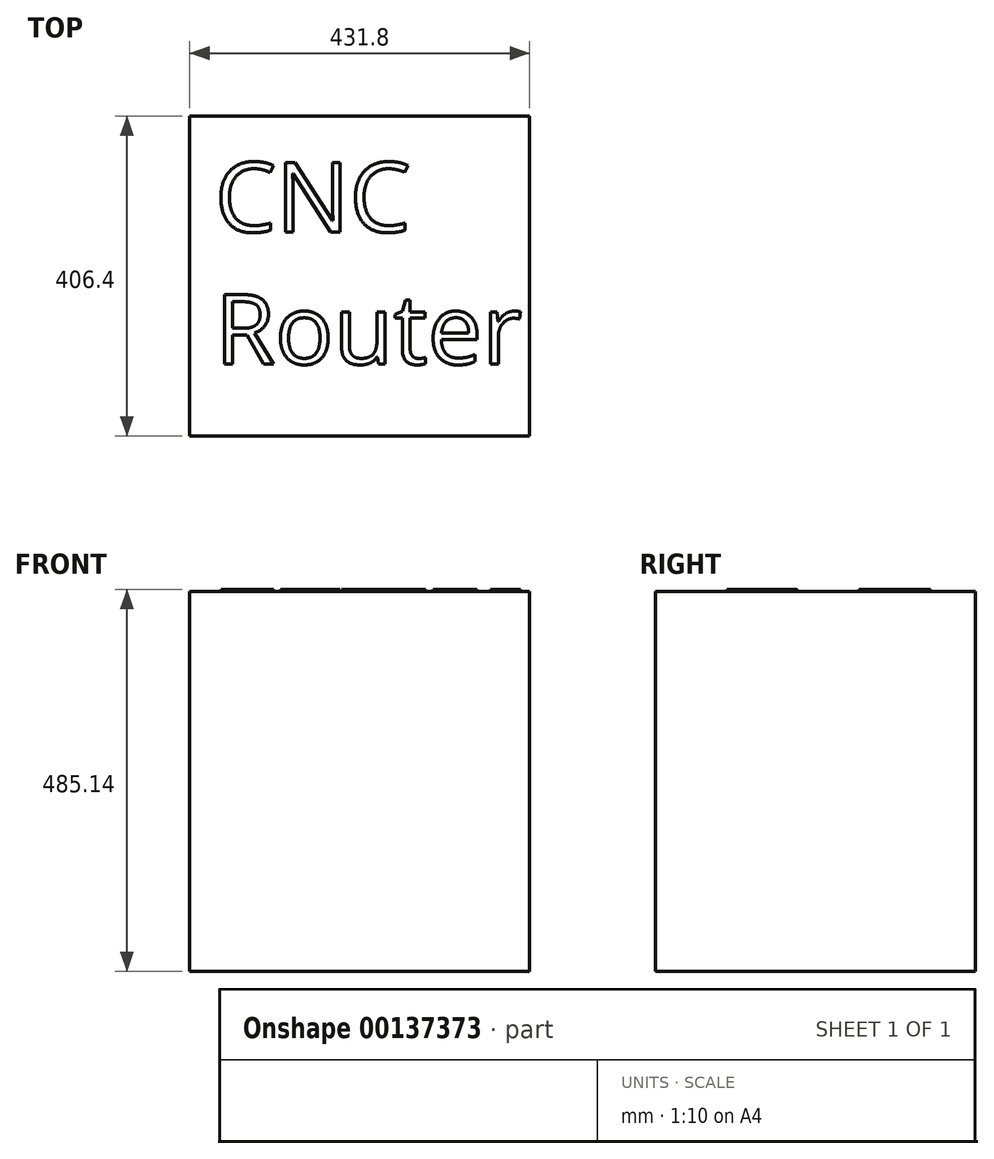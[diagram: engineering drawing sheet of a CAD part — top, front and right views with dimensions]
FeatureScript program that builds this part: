
annotation { "Feature Type Name" : "Feature", "Feature Type Description" : "" }
export const myFeature = defineFeature(function(context is Context, id is Id, definition is map)
    precondition{}
    {
        {
            var Q0;
            Q0=qCreatedBy(makeId("Top.planeOp"),FACE);
            var sketch = newSketch(context, id + "F0", { "sketchPlane" : qUnion([Q0])});
            skLineSegment(sketch, "E0.bottom", {"start": v(-209.66, 203.2) * mm, "end": v(222.14, 203.2) * mm});
            skLineSegment(sketch, "E0.top", {"start": v(-209.66, -203.2) * mm, "end": v(222.14, -203.2) * mm});
            skLineSegment(sketch, "E0.left", {"start": v(-209.66, 203.2) * mm, "end": v(-209.66, -203.2) * mm});
            skLineSegment(sketch, "E0.right", {"start": v(222.14, 203.2) * mm, "end": v(222.14, -203.2) * mm});
            skPoint(sketch, "E0.middle", {"position": v(6.24, 0) * mm});
            skSolve(sketch);
        }
        {
            var Q0;
            Q0 = qSketchRegion(id + "F0", true);
            extrude(context, id + "F1", {"entities" : qUnion([Q0]), "depth" : 482.6 * mm});
        }
        {
            var Q0;
            Q0=makeQuery(id+"F1.opExtrude","CAP_FACE",FACE,{"disambiguationData":[OSD([sQuery(id+"F0.wireOp",EDGE,"E0.bottom"),sQuery(id+"F0.wireOp",EDGE,"E0.top"),sQuery(id+"F0.wireOp",EDGE,"E0.left"),sQuery(id+"F0.wireOp",EDGE,"E0.right")])],"isStart":false});
            var sketch = newSketch(context, id + "F2", { "sketchPlane" : qUnion([Q0])});
            skText(sketch, "E1", { "text": "CNC \nRouter", "fontName": "OpenSans-Regular.ttf"});
            const initialGuessF2  = {"E1": [-0.1778, 0.05615, 1, 0, 0.0889]};
            skSetInitialGuess(sketch, initialGuessF2);
            skSolve(sketch);
        }
        {
            var Q0;
            Q0 = qSketchRegion(id + "F2", true);
            extrude(context, id + "F3", {"entities" : qUnion([Q0]), "operationType" : NewBodyOperationType.ADD, "depth" : 2.54 * mm});
        }
    });
